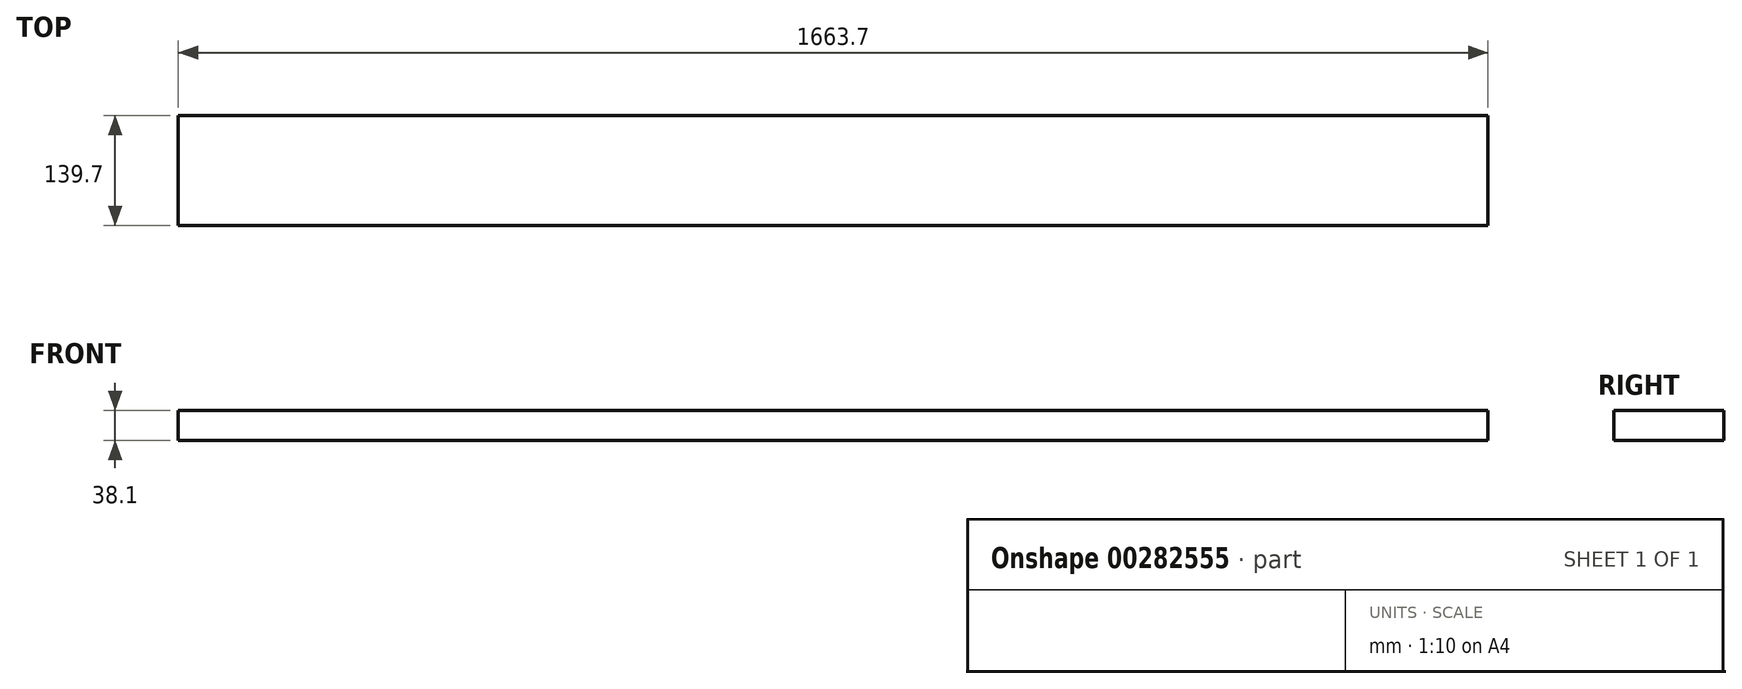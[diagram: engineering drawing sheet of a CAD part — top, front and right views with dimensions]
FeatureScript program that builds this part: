
annotation { "Feature Type Name" : "Feature", "Feature Type Description" : "" }
export const myFeature = defineFeature(function(context is Context, id is Id, definition is map)
    precondition{}
    {
        {
            var Q0;
            Q0=qCreatedBy(makeId("Right.planeOp"),FACE);
            var sketch = newSketch(context, id + "F0", { "sketchPlane" : qUnion([Q0])});
            skLineSegment(sketch, "E0.bottom", {"start": v(0, 0) * mm, "end": v(-139.7, 0) * mm});
            skLineSegment(sketch, "E0.top", {"start": v(0, 38.1) * mm, "end": v(-139.7, 38.1) * mm});
            skLineSegment(sketch, "E0.left", {"start": v(0, 0) * mm, "end": v(0, 38.1) * mm});
            skLineSegment(sketch, "E0.right", {"start": v(-139.7, 0) * mm, "end": v(-139.7, 38.1) * mm});
            skSolve(sketch);
        }
        {
            var Q0;
            Q0=makeQuery(id+"F0.imprint","IMPRINT",FACE,{"disambiguationData":[TD([[makeQuery(id+"F0.imprint","IMPRINT",EDGE,{"derivedFrom":sQuery(id+"F0.wireOp",EDGE,"E0.bottom")}),-1.0]])]});
            extrude(context, id + "F1", {"entities" : qUnion([Q0]), "depth" : 1663.7 * mm});
        }
    });
